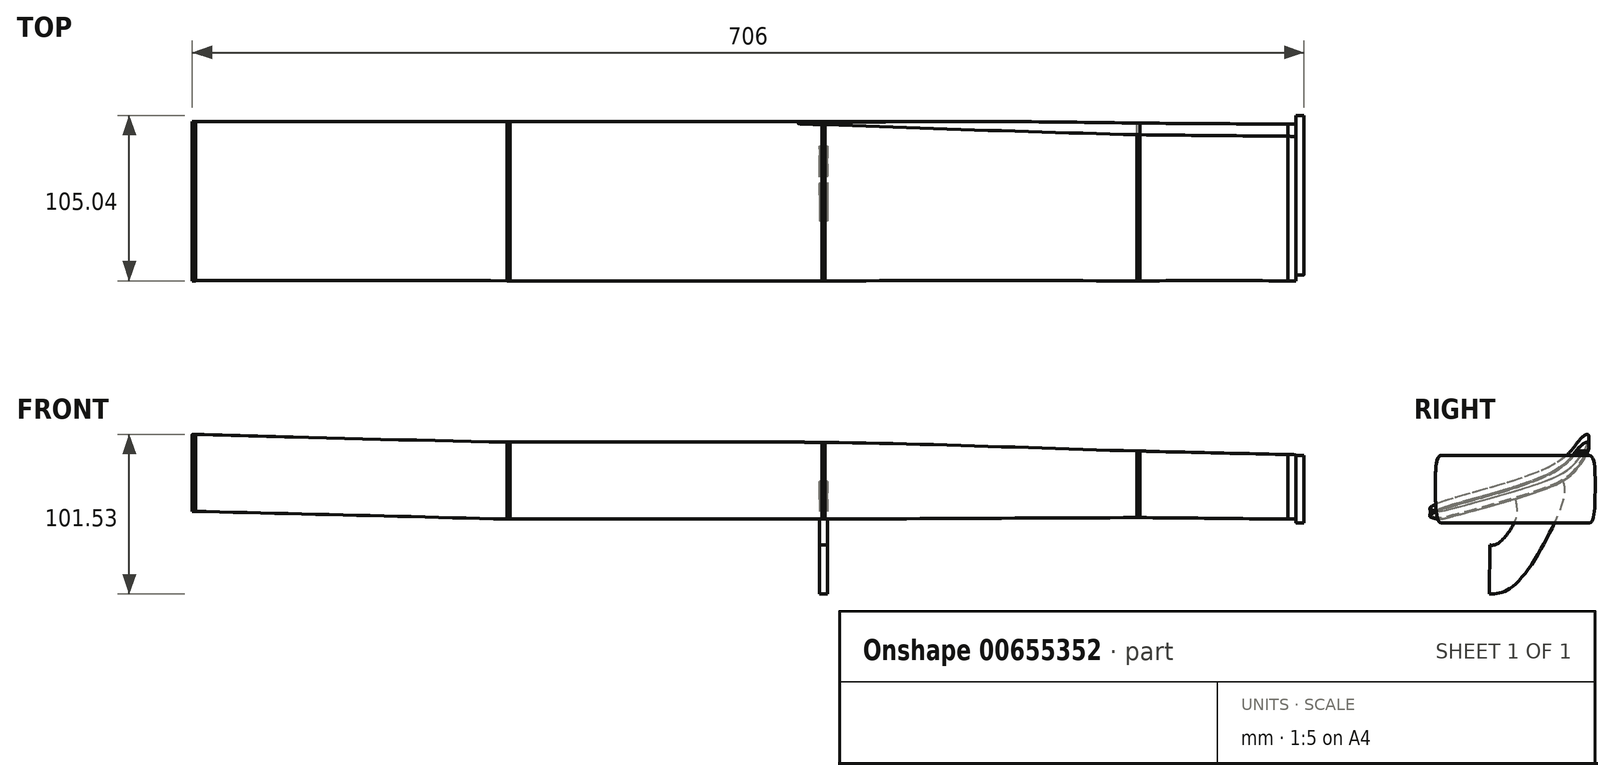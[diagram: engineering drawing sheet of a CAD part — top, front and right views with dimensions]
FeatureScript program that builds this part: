
annotation { "Feature Type Name" : "Feature", "Feature Type Description" : "" }
export const myFeature = defineFeature(function(context is Context, id is Id, definition is map)
    precondition{}
    {
        {
            var Q0;
            Q0=qCreatedBy(makeId("Right.planeOp"),FACE);
            cPlane(context, id + "F0", {"entities" : qUnion([Q0]), "cplaneType" : CPlaneType.OFFSET, "offset" : 700 * mm, "width" : 152.4 * mm, "height" : 152.4 * mm});
        }
        {
            var Q0;
            Q0=qCreatedBy(id+"F0.planeOp",FACE);
            var sketch = newSketch(context, id + "F1", { "sketchPlane" : qUnion([Q0])});
            skLineSegment(sketch, "E0", {"start": v(-47.02, 21.39) * mm, "end": v(47.02, 21.39) * mm});
            skLineSegment(sketch, "E1.MirrorCS", {"start": v(-47.02, -21.39) * mm, "end": v(47.02, -21.39) * mm});
            skFitSpline(sketch, "E2", {"points": [v(-47.02, 21.39) * mm, v(-50.7, 0) * mm, v(-47.02, -21.39) * mm], "startDerivative": vector(-22.95, 0) * mm, "endDerivative": vector(21.25, 0) * mm});
            skFitSpline(sketch, "E3.MirrorCS", {"points": [v(47.02, 21.39) * mm, v(50.7, 0) * mm, v(47.02, -21.39) * mm], "startDerivative": vector(22.95, 0) * mm, "endDerivative": vector(-21.25, 0) * mm});
            skSolve(sketch);
        }
        {
            var Q0;
            Q0 = qSketchRegion(id + "F1", true);
            extrude(context, id + "F2", {"entities" : qUnion([Q0]), "depth" : 5 * mm, "offsetDistance" : 25 * mm});
        }
        {
            var Q0;
            Q0=qCreatedBy(id+"F0.planeOp",FACE);
            cPlane(context, id + "F3", {"entities" : qUnion([Q0]), "cplaneType" : CPlaneType.OFFSET, "offset" : 100 * mm, "oppositeDirection" : true, "width" : 150 * mm, "height" : 150 * mm});
        }
        {
            var Q0;
            Q0=qCreatedBy(id+"F0.planeOp",FACE);
            cPlane(context, id + "F4", {"entities" : qUnion([Q0]), "cplaneType" : CPlaneType.OFFSET, "offset" : 300 * mm, "oppositeDirection" : true, "width" : 150 * mm, "height" : 150 * mm});
        }
        {
            var Q0;
            Q0=qCreatedBy(id+"F0.planeOp",FACE);
            cPlane(context, id + "F5", {"entities" : qUnion([Q0]), "cplaneType" : CPlaneType.OFFSET, "offset" : 500 * mm, "oppositeDirection" : true, "width" : 150 * mm, "height" : 150 * mm});
        }
        {
            var Q0;
            Q0=qCreatedBy(id+"F3.planeOp",FACE);
            var sketch = newSketch(context, id + "F6", { "sketchPlane" : qUnion([Q0])});
            skFitSpline(sketch, "E4", {"points": [v(41.74, 27.19) * mm, v(33.52, 17.27) * mm, v(15.4, 6.23) * mm, v(-23.42, -6.24) * mm, v(-44.1, -12.19) * mm, v(-51.46, -15.02) * mm, v(-54.3, -17.28) * mm, v(-49.48, -18.98) * mm, v(-42.96, -18.13) * mm, v(19.92, 0.42) * mm, v(38.05, 11.6) * mm, v(45.42, 22.37) * mm, v(46.84, 26.9) * mm, v(45.99, 29.74) * mm, v(41.74, 27.19) * mm]});
            skSolve(sketch);
        }
        {
            var Q0;
            Q0=qCreatedBy(id+"F4.planeOp",FACE);
            var sketch = newSketch(context, id + "F7", { "sketchPlane" : qUnion([Q0])});
            skFitSpline(sketch, "E5", {"points": [v(41.74, 27.19) * mm, v(33.52, 17.27) * mm, v(15.4, 6.23) * mm, v(-23.42, -6.24) * mm, v(-44.1, -12.19) * mm, v(-51.46, -15.02) * mm, v(-54.3, -17.28) * mm, v(-49.48, -18.98) * mm, v(-42.96, -18.13) * mm, v(19.92, 0.42) * mm, v(38.05, 11.6) * mm, v(45.42, 22.37) * mm, v(46.84, 26.9) * mm, v(45.99, 29.74) * mm, v(41.74, 27.19) * mm]});
            skSolve(sketch);
        }
        {
            var Q0;
            Q0=qCreatedBy(id+"F5.planeOp",FACE);
            var sketch = newSketch(context, id + "F8", { "sketchPlane" : qUnion([Q0])});
            skFitSpline(sketch, "E6", {"points": [v(41.74, 27.19) * mm, v(33.52, 17.27) * mm, v(15.4, 6.23) * mm, v(-23.42, -6.24) * mm, v(-44.1, -12.19) * mm, v(-51.46, -15.02) * mm, v(-54.3, -17.28) * mm, v(-49.48, -18.98) * mm, v(-42.96, -18.13) * mm, v(19.92, 0.42) * mm, v(38.05, 11.6) * mm, v(45.42, 22.37) * mm, v(46.84, 26.9) * mm, v(45.99, 29.74) * mm, v(41.74, 27.19) * mm]});
            skSolve(sketch);
        }
        {
            var Q0;
            Q0=qCreatedBy(makeId("Right.planeOp"),FACE);
            var sketch = newSketch(context, id + "F9", { "sketchPlane" : qUnion([Q0])});
            skFitSpline(sketch, "E7", {"points": [v(41.74, 27.19) * mm, v(33.52, 17.27) * mm, v(15.4, 6.23) * mm, v(-23.42, -6.24) * mm, v(-44.1, -12.19) * mm, v(-51.46, -15.02) * mm, v(-54.3, -17.28) * mm, v(-49.48, -18.98) * mm, v(-42.96, -18.13) * mm, v(19.92, 0.42) * mm, v(38.05, 11.6) * mm, v(45.42, 22.37) * mm, v(46.84, 26.9) * mm, v(45.99, 29.74) * mm, v(41.74, 27.19) * mm]});
            skSolve(sketch);
        }
        {
            var Q0;
            Q0=qCreatedBy(id+"F0.planeOp",FACE);
            var sketch = newSketch(context, id + "F10", { "sketchPlane" : qUnion([Q0])});
            skFitSpline(sketch, "E8", {"points": [v(41.74, 27.19) * mm, v(33.52, 17.27) * mm, v(15.4, 6.23) * mm, v(-23.42, -6.24) * mm, v(-44.1, -12.19) * mm, v(-51.46, -15.02) * mm, v(-54.3, -17.28) * mm, v(-49.48, -18.98) * mm, v(-42.96, -18.13) * mm, v(19.92, 0.42) * mm, v(38.05, 11.6) * mm, v(45.42, 22.37) * mm, v(46.84, 26.9) * mm, v(45.99, 29.74) * mm, v(41.74, 27.19) * mm]});
            skSolve(sketch);
        }
        {
            var Q0;
            Q0=makeQuery(id+"F6.imprint","IMPRINT",FACE,{"disambiguationData":[TD([[makeQuery(id+"F6.imprint","IMPRINT",EDGE,{"derivedFrom":sQuery(id+"F6.wireOp",EDGE,"E4")}),1.0]])]});
            var Q1;
            Q1=sQuery(id+"F6.wireOp",EDGE,"E4");
            extrude(context, id + "F11", {"entities" : qUnion([Q0]), "surfaceEntities" : qUnion([Q1]), "endBound" : BoundingType.SYMMETRIC, "depth" : 2 * mm, "offsetDistance" : 25 * mm});
        }
        {
            var Q0;
            Q0=makeQuery(id+"F10.imprint","IMPRINT",FACE,{"disambiguationData":[TD([[makeQuery(id+"F10.imprint","IMPRINT",EDGE,{"derivedFrom":sQuery(id+"F10.wireOp",EDGE,"E8")}),1.0]])]});
            extrude(context, id + "F12", {"entities" : qUnion([Q0]), "operationType" : NewBodyOperationType.ADD, "oppositeDirection" : true, "depth" : 5 * mm, "offsetDistance" : 25 * mm});
        }
        {
            var Q0;
            Q0=makeQuery(id+"F11.opExtrude","SWEPT_BODY",BODY,{"disambiguationData":[OSD([sQuery(id+"F6.wireOp",EDGE,"E4")])]});
            transform(context, id + "F13", {"entities" : qUnion([Q0]), "transformType" : TransformType.TRANSLATION_3D, "dx" : 0 * mm, "dy" : 0 * mm, "dz" : 1 * mm, "makeCopy" : false});
        }
        {
            var Q0;
            Q0=makeQuery(id+"F12.opExtrude","CAP_FACE",FACE,{"disambiguationData":[OSD([sQuery(id+"F10.wireOp",EDGE,"E8")])],"isStart":false});
            var Q1;
            Q1=makeQuery(id+"F11.opExtrude","CAP_FACE",FACE,{"disambiguationData":[OSD([sQuery(id+"F6.wireOp",EDGE,"E4")])],"isStart":false});
            loft(context, id + "F14", {"sheetProfilesArray" : [{ "sheetProfileEntities" : qUnion([Q0]) }, { "sheetProfileEntities" : qUnion([Q1]) }]});
        }
        {
            var Q0;
            Q0 = qSketchRegion(id + "F7", true);
            var Q1;
            Q1 = qSketchRegion(id + "F8", true);
            var Q2;
            Q2 = qSketchRegion(id + "F9", true);
            extrude(context, id + "F15", {"entities" : qUnion([Q0, Q1, Q2]), "endBound" : BoundingType.SYMMETRIC, "depth" : 2 * mm, "offsetDistance" : 25 * mm});
        }
        {
            var Q1;
            Q1=makeQuery(id+"F11.opExtrude","CAP_FACE",FACE,{"disambiguationData":[OSD([sQuery(id+"F6.wireOp",EDGE,"E4")])],"isStart":true});
            var Q2;
            Q2=makeQuery(id+"F15.opExtrude","CAP_FACE",FACE,{"disambiguationData":[OSD([sQuery(id+"F7.wireOp",EDGE,"E5")])],"isStart":false});
            loft(context, id + "F16", {"operationType" : NewBodyOperationType.ADD, "sheetProfilesArray" : [{ "sheetProfileEntities" : qUnion([Q1]) }, { "sheetProfileEntities" : qUnion([Q2]) }]});
        }
        {
            var Q0;
            Q0=makeQuery(id+"F15.opExtrude","CAP_FACE",FACE,{"disambiguationData":[OSD([sQuery(id+"F8.wireOp",EDGE,"E6")])],"isStart":false});
            var Q1;
            Q1=makeQuery(id+"F15.opExtrude","CAP_FACE",FACE,{"disambiguationData":[OSD([sQuery(id+"F7.wireOp",EDGE,"E5")])],"isStart":true});
            loft(context, id + "F17", {"sheetProfilesArray" : [{ "sheetProfileEntities" : qUnion([Q0]) }, { "sheetProfileEntities" : qUnion([Q1]) }]});
        }
        {
            var Q0;
            Q0=qCreatedBy(makeId("Front.planeOp"),FACE);
            var sketch = newSketch(context, id + "F18", { "sketchPlane" : qUnion([Q0])});
            skFitSpline(sketch, "E9", {"points": [v(0, 30.37) * mm, v(123.11, 29.66) * mm, v(398.26, 29.66) * mm, v(559.06, 25.37) * mm, v(700.56, 21.8) * mm], "startDerivative": vector(503.89, -5.3) * mm, "endDerivative": vector(628.74, -14.05) * mm});
            skLineSegment(sketch, "E10", {"start": v(700.56, 21.8) * mm, "end": v(700.56, 51.81) * mm});
            skLineSegment(sketch, "E11", {"start": v(700.56, 51.81) * mm, "end": v(0, 30.37) * mm});
            skSolve(sketch);
        }
        {
            var Q0;
            Q0 = qSketchRegion(id + "F18", true);
            extrude(context, id + "F19", {"entities" : qUnion([Q0]), "operationType" : NewBodyOperationType.REMOVE, "oppositeDirection" : true, "depth" : 107 * mm, "offsetDistance" : 25 * mm});
        }
        {
            var Q0;
            Q0=qCreatedBy(id+"F4.planeOp",FACE);
            var sketch = newSketch(context, id + "F20", { "sketchPlane" : qUnion([Q0])});
            skFitSpline(sketch, "E12", {"points": [v(30.31, 4.96) * mm, v(30.31, -6.94) * mm, v(0, -60.48) * mm, v(-16.43, -66.71) * mm], "startDerivative": vector(10.26, -39.77) * mm, "endDerivative": vector(-56.78, -3.22) * mm});
            skFitSpline(sketch, "E13", {"points": [v(0, -6.66) * mm, v(0, -19.4) * mm, v(-11.3, -34.7) * mm, v(-16.15, -35.55) * mm], "startDerivative": vector(6.86, -33.79) * mm, "endDerivative": vector(-20.05, 1.95) * mm});
            skLineSegment(sketch, "E14", {"start": v(-16.15, -35.55) * mm, "end": v(-16.43, -66.71) * mm});
            skLineSegment(sketch, "E15", {"start": v(0, -6.66) * mm, "end": v(17.85, 0) * mm});
            skLineSegment(sketch, "E16", {"start": v(17.85, 0) * mm, "end": v(30.31, 4.96) * mm});
            skSolve(sketch);
        }
        {
            var Q0;
            Q0 = qSketchRegion(id + "F20", true);
            extrude(context, id + "F21", {"entities" : qUnion([Q0]), "endBound" : BoundingType.SYMMETRIC, "depth" : 5 * mm, "offsetDistance" : 25 * mm});
        }
        {
            var Q0;
            Q0=makeQuery(id+"F15.opExtrude","SWEPT_BODY",BODY,{"disambiguationData":[OSD([sQuery(id+"F9.wireOp",EDGE,"E7")])]});
            transform(context, id + "F22", {"entities" : qUnion([Q0]), "transformType" : TransformType.TRANSLATION_3D, "dx" : 0 * mm, "dy" : 0 * mm, "dz" : 5 * mm, "makeCopy" : false});
        }
        {
            var Q0;
            Q0=makeQuery(id+"F15.opExtrude","CAP_FACE",FACE,{"disambiguationData":[OSD([sQuery(id+"F9.wireOp",EDGE,"E7")])],"isStart":true});
            var Q1;
            Q1=makeQuery(id+"F15.opExtrude","CAP_FACE",FACE,{"disambiguationData":[OSD([sQuery(id+"F8.wireOp",EDGE,"E6")])],"isStart":true});
            loft(context, id + "F23", {"sheetProfilesArray" : [{ "sheetProfileEntities" : qUnion([Q0]) }, { "sheetProfileEntities" : qUnion([Q1]) }]});
        }
    });
